# Revit family: 103.501.851_Arres 3.0  Premium Schneefang-Blindmodul
name_source: partatom
category: Allgemeines Modell
units: mm (PartAtom-declared; Revit-internal decimal feet)

## family parameters
Arbeitsebenenbasiert = Nein
Beim Laden mit Abzugskörper schneiden = Nein
Bemaßung runder Anschluss = Durchmesser verwenden
Gemeinsam genutzt = Nein
Immer vertikal = Ja
Kann Basisbauteil für Bewehrung sein = Nein
Raumberechnungspunkt = Nein
Teiletyp = Normal

## types (1)
- Norm
    Beschreibung = Arres 3.0 Premium Schneefang-Blindmodul
    Breite = 460 mm
    Farbe = RAL 9005 matt (schwarz)
    Gewicht = 10,9 kg
    Hersteller = Solarmarkt GmbH
    Homepage = https://www.arres.ch
    Höhe = 20 mm
    Länge = 1691 mm
    Material = Aluminium
    Modell = Arres 3.0 Premium Schneefang-Blindmodul
    System = Indach
    URL = https://www.solarmarkt.ch
    Vorgabe-Ansicht = 0 mm  [stored 0 ft]

note: [stored X ft] marks values corroborated as IEEE doubles in the binary element streams (Revit-internal decimal feet)
